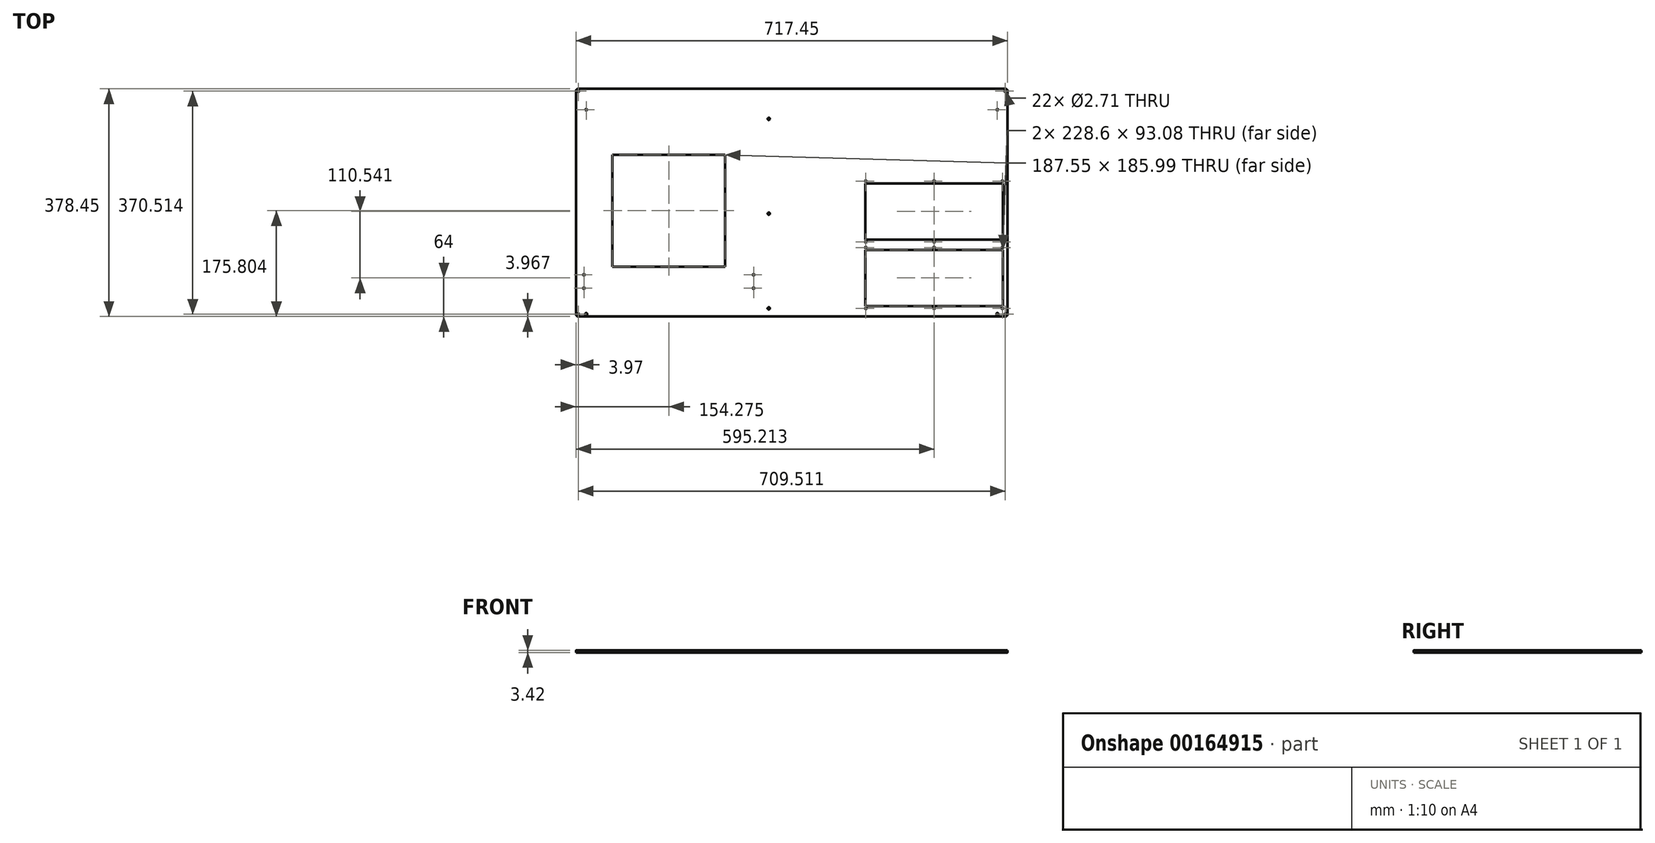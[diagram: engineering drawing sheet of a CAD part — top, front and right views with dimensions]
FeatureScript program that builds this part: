
annotation { "Feature Type Name" : "Feature", "Feature Type Description" : "" }
export const myFeature = defineFeature(function(context is Context, id is Id, definition is map)
    precondition{}
    {
        {
            var Q0;
            Q0=qCreatedBy(makeId("Top.planeOp"),FACE);
            var sketch = newSketch(context, id + "F0", { "sketchPlane" : qUnion([Q0])});
            skLineSegment(sketch, "E0.bottom", {"start": v(0, 0) * mm, "end": v(-717.45, 0) * mm});
            skLineSegment(sketch, "E0.top", {"start": v(0, -378.45) * mm, "end": v(-717.45, -378.45) * mm});
            skLineSegment(sketch, "E0.left", {"start": v(0, 0) * mm, "end": v(0, -378.45) * mm});
            skLineSegment(sketch, "E0.right", {"start": v(-717.45, 0) * mm, "end": v(-717.45, -378.45) * mm});
            skSolve(sketch);
        }
        {
            var Q0;
            Q0=qSketchRegion(id+"F0",true);
            extrude(context, id + "F1", {"entities" : qUnion([Q0]), "depth" : 3.42 * mm});
        }
        {
            var Q0;
            Q0=makeQuery(id+"F1.opExtrude","SWEPT_EDGE",EDGE,{"disambiguationData":[OSD([sQuery(id+"F0.wireOp",EDGE,"E0.bottom"),sQuery(id+"F0.wireOp",EDGE,"E0.right")])]});
            var Q1;
            Q1=makeQuery(id+"F1.opExtrude","SWEPT_EDGE",EDGE,{"disambiguationData":[OSD([sQuery(id+"F0.wireOp",EDGE,"E0.top"),sQuery(id+"F0.wireOp",EDGE,"E0.right")])]});
            var Q2;
            Q2=makeQuery(id+"F1.opExtrude","SWEPT_EDGE",EDGE,{"disambiguationData":[OSD([sQuery(id+"F0.wireOp",EDGE,"E0.top"),sQuery(id+"F0.wireOp",EDGE,"E0.left")])]});
            var Q3;
            Q3=makeQuery(id+"F1.opExtrude","SWEPT_EDGE",EDGE,{"disambiguationData":[OSD([sQuery(id+"F0.wireOp",EDGE,"E0.bottom"),sQuery(id+"F0.wireOp",EDGE,"E0.left")])]});
            fillet(context, id + "F2", {"entities" : qUnion([Q0, Q1, Q2, Q3]), "radius" : 3.97 * mm, "tangentPropagation" : true, "allowEdgeOverflow" : false});
        }
        {
            var Q0;
            Q0=makeQuery(id+"F1.opExtrude","CAP_FACE",FACE,{"disambiguationData":[OSD([sQuery(id+"F0.wireOp",EDGE,"E0.bottom"),sQuery(id+"F0.wireOp",EDGE,"E0.top"),sQuery(id+"F0.wireOp",EDGE,"E0.left"),sQuery(id+"F0.wireOp",EDGE,"E0.right")])],"isStart":false});
            var sketch = newSketch(context, id + "F3", { "sketchPlane" : qUnion([Q0])});
            skCircle(sketch, "E1", {"center": v(-713.48, -3.97) * mm, "radius": 1.35 * mm});
            skCircle(sketch, "E2", {"center": v(-3.97, -3.97) * mm, "radius": 1.35 * mm});
            skCircle(sketch, "E3", {"center": v(-713.48, -374.48) * mm, "radius": 1.35 * mm});
            skCircle(sketch, "E4", {"center": v(-3.97, -374.48) * mm, "radius": 1.35 * mm});
            skLineSegment(sketch, "E5", {"start": v(-422.2, -320.25) * mm, "end": v(-704.15, -320.25) * mm, "construction": true});
            skLineSegment(sketch, "E6", {"start": v(-422.2, -309.1) * mm, "end": v(-422.2, -331.4) * mm, "construction": true});
            skLineSegment(sketch, "E7", {"start": v(-704.15, -309.1) * mm, "end": v(-704.15, -331.4) * mm, "construction": true});
            skCircle(sketch, "E8", {"center": v(-704.15, -309.1) * mm, "radius": 1.35 * mm});
            skCircle(sketch, "E9", {"center": v(-704.15, -331.4) * mm, "radius": 1.35 * mm});
            skCircle(sketch, "E10", {"center": v(-422.2, -331.4) * mm, "radius": 1.35 * mm});
            skCircle(sketch, "E11", {"center": v(-422.2, -309.1) * mm, "radius": 1.35 * mm});
            skLineSegment(sketch, "E12", {"start": v(-563.18, -320.25) * mm, "end": v(-563.18, -378.45) * mm, "construction": true});
            skLineSegment(sketch, "E13", {"start": v(-3.97, -374.48) * mm, "end": v(-17.16, -374.48) * mm, "construction": true});
            skLineSegment(sketch, "E14", {"start": v(-713.48, -374.48) * mm, "end": v(-700.3, -374.48) * mm, "construction": true});
            skCircle(sketch, "E15", {"center": v(-17.16, -374.48) * mm, "radius": 1.83 * mm});
            skCircle(sketch, "E16", {"center": v(-700.3, -374.48) * mm, "radius": 1.83 * mm});
            skLineSegment(sketch, "E17", {"start": v(-358.72, 0) * mm, "end": v(-358.72, -34.63) * mm, "construction": true});
            skLineSegment(sketch, "E18", {"start": v(-700.3, -34.63) * mm, "end": v(-17.16, -34.63) * mm, "construction": true});
            skCircle(sketch, "E19", {"center": v(-700.3, -34.63) * mm, "radius": 1.35 * mm});
            skCircle(sketch, "E20", {"center": v(-17.16, -34.63) * mm, "radius": 1.35 * mm});
            skLineSegment(sketch, "E21", {"start": v(-397, -34.63) * mm, "end": v(-397, -49.96) * mm, "construction": true});
            skLineSegment(sketch, "E22", {"start": v(-397, -49.96) * mm, "end": v(-422.2, -49.96) * mm, "construction": true});
            skLineSegment(sketch, "E23", {"start": v(-422.2, -309.1) * mm, "end": v(-422.2, -49.96) * mm, "construction": true});
            skCircle(sketch, "E24", {"center": v(-397, -49.96) * mm, "radius": 1.83 * mm});
            skLineSegment(sketch, "E25", {"start": v(-563.18, -320.25) * mm, "end": v(-563.18, -295.64) * mm, "construction": true});
            skLineSegment(sketch, "E26.bottom", {"start": v(-469.4, -295.64) * mm, "end": v(-656.95, -295.64) * mm});
            skLineSegment(sketch, "E26.top", {"start": v(-469.4, -109.65) * mm, "end": v(-656.95, -109.65) * mm});
            skLineSegment(sketch, "E26.left", {"start": v(-469.4, -295.64) * mm, "end": v(-469.4, -109.65) * mm});
            skLineSegment(sketch, "E26.right", {"start": v(-656.95, -295.64) * mm, "end": v(-656.95, -109.65) * mm});
            skLineSegment(sketch, "E27.bottom", {"start": v(-7.94, -360.99) * mm, "end": v(-236.54, -360.99) * mm});
            skLineSegment(sketch, "E27.top", {"start": v(-7.94, -267.91) * mm, "end": v(-236.54, -267.91) * mm});
            skLineSegment(sketch, "E27.left", {"start": v(-7.94, -360.99) * mm, "end": v(-7.94, -267.91) * mm});
            skLineSegment(sketch, "E27.right", {"start": v(-236.54, -360.99) * mm, "end": v(-236.54, -267.91) * mm});
            skLineSegment(sketch, "E28", {"start": v(-122.24, -360.99) * mm, "end": v(-122.24, -364.96) * mm, "construction": true});
            skLineSegment(sketch, "E29", {"start": v(-235.74, -364.96) * mm, "end": v(-8.73, -364.96) * mm, "construction": true});
            skCircle(sketch, "E30", {"center": v(-235.74, -364.96) * mm, "radius": 1.35 * mm});
            skCircle(sketch, "E31", {"center": v(-122.24, -364.96) * mm, "radius": 1.35 * mm});
            skCircle(sketch, "E32", {"center": v(-8.73, -364.96) * mm, "radius": 1.35 * mm});
            skLineSegment(sketch, "E33", {"start": v(-7.94, -314.45) * mm, "end": v(0, -314.45) * mm, "construction": true});
            skLineSegment(sketch, "E34", {"start": v(-122.24, -364.96) * mm, "end": v(-122.24, -378.45) * mm, "construction": true});
            skLineSegment(sketch, "E35", {"start": v(-122.24, -267.91) * mm, "end": v(-122.24, -263.94) * mm, "construction": true});
            skLineSegment(sketch, "E36", {"start": v(-235.74, -263.94) * mm, "end": v(-8.73, -263.94) * mm, "construction": true});
            skCircle(sketch, "E37", {"center": v(-235.74, -263.94) * mm, "radius": 1.35 * mm});
            skCircle(sketch, "E38", {"center": v(-122.24, -263.94) * mm, "radius": 1.35 * mm});
            skCircle(sketch, "E39", {"center": v(-8.73, -263.94) * mm, "radius": 1.35 * mm});
            skLineSegment(sketch, "E40.bottom", {"start": v(-7.94, -250.45) * mm, "end": v(-236.54, -250.45) * mm});
            skLineSegment(sketch, "E40.top", {"start": v(-7.94, -157.37) * mm, "end": v(-236.54, -157.37) * mm});
            skLineSegment(sketch, "E40.left", {"start": v(-7.94, -250.45) * mm, "end": v(-7.94, -157.37) * mm});
            skLineSegment(sketch, "E40.right", {"start": v(-236.54, -250.45) * mm, "end": v(-236.54, -157.37) * mm});
            skPoint(sketch, "E40.middle", {"position": v(-122.24, -203.9) * mm});
            skLineSegment(sketch, "E41.bottom", {"start": v(-8.73, -254.42) * mm, "end": v(-235.74, -254.42) * mm, "construction": true});
            skLineSegment(sketch, "E41.top", {"start": v(-8.73, -153.4) * mm, "end": v(-235.74, -153.4) * mm, "construction": true});
            skLineSegment(sketch, "E41.left", {"start": v(-8.73, -254.42) * mm, "end": v(-8.73, -153.4) * mm, "construction": true});
            skLineSegment(sketch, "E41.right", {"start": v(-235.74, -254.42) * mm, "end": v(-235.74, -153.4) * mm, "construction": true});
            skLineSegment(sketch, "E42", {"start": v(-235.74, -364.96) * mm, "end": v(-235.74, -263.94) * mm, "construction": true});
            skLineSegment(sketch, "E43", {"start": v(-8.73, -263.94) * mm, "end": v(-8.73, -364.96) * mm, "construction": true});
            skLineSegment(sketch, "E44", {"start": v(-122.24, -263.94) * mm, "end": v(-122.24, -254.42) * mm, "construction": true});
            skCircle(sketch, "E45", {"center": v(-235.74, -254.42) * mm, "radius": 1.35 * mm});
            skCircle(sketch, "E46", {"center": v(-122.24, -254.42) * mm, "radius": 1.35 * mm});
            skCircle(sketch, "E47", {"center": v(-8.73, -254.42) * mm, "radius": 1.35 * mm});
            skCircle(sketch, "E48", {"center": v(-8.73, -153.4) * mm, "radius": 1.35 * mm});
            skCircle(sketch, "E49", {"center": v(-235.74, -153.4) * mm, "radius": 1.35 * mm});
            skCircle(sketch, "E50", {"center": v(-122.24, -153.4) * mm, "radius": 1.35 * mm});
            skLineSegment(sketch, "E51", {"start": v(-397, -49.96) * mm, "end": v(-397, -364.96) * mm, "construction": true});
            skCircle(sketch, "E52", {"center": v(-397, -207.46) * mm, "radius": 1.83 * mm});
            skCircle(sketch, "E53", {"center": v(-397, -364.96) * mm, "radius": 1.83 * mm});
            skSolve(sketch);
        }
        {
            var Q0;
            Q0 = qSketchRegion(id + "F3", true);
            var Q1;
            Q1=makeQuery(id+"F1.opExtrude","CAP_FACE",FACE,{"disambiguationData":[OSD([sQuery(id+"F0.wireOp",EDGE,"E0.bottom"),sQuery(id+"F0.wireOp",EDGE,"E0.top"),sQuery(id+"F0.wireOp",EDGE,"E0.left"),sQuery(id+"F0.wireOp",EDGE,"E0.right")])],"isStart":true});
            extrude(context, id + "F4", {"entities" : qUnion([Q0]), "operationType" : NewBodyOperationType.REMOVE, "endBound" : BoundingType.UP_TO_SURFACE, "oppositeDirection" : true, "endBoundEntityFace" : qUnion([Q1]), "depth" : 25.4 * mm});
        }
    });
